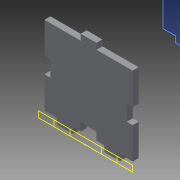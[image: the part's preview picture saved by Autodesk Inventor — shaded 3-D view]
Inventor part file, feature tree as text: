
AUTODESK INVENTOR PART (.ipt)
format: ipt  version: 2015 SP1 (Build 190203100, 203)  size: 138,240 bytes
history: native  units: in
note: dims shown in document units (in); Inventor stores cm internally (conversion verified against a paired STEP export)
features: reference x7, sketch x4, extrude x3, plane x1
ambient origin geometry x8: Origin, YZ Plane, XZ Plane, XY Plane, X Axis, Y Axis, Z Axis, Center Point
bodies: Solid1 (feature_tree)
feature tree (15):
  sketch  "Sketch1"  dims[d0=2.0in d2=0.5in]
  plane  "Work Plane1"
  extrude  "Extrusion1"  Depth=0.5in
  extrude  "Extrusion2"  Depth=0.19in TaperAngle=0.0deg
  extrude  "Extrusion3"  Depth=0.19in
  reference  "Reference1"
  reference  "Reference2"
  reference  "Reference3"
  sketch  "Sketch2"  dims[d5=0.19in d6=0.19in d7=0.0in]
  reference  "Reference4"
  reference  "Reference5"
  reference  "Reference6"
  reference  "Reference7"
  sketch  "Sketch3"  dims[d8=0.5in d9=0.19in]
  sketch  "Sketch4"  dims[d10=1.15in d11=0.19in d12=0.0in d13=0.5in d14=0.25in d15=1.15in d16=0.19in d17=0.0in d18=0.75in d19=0.75in]
